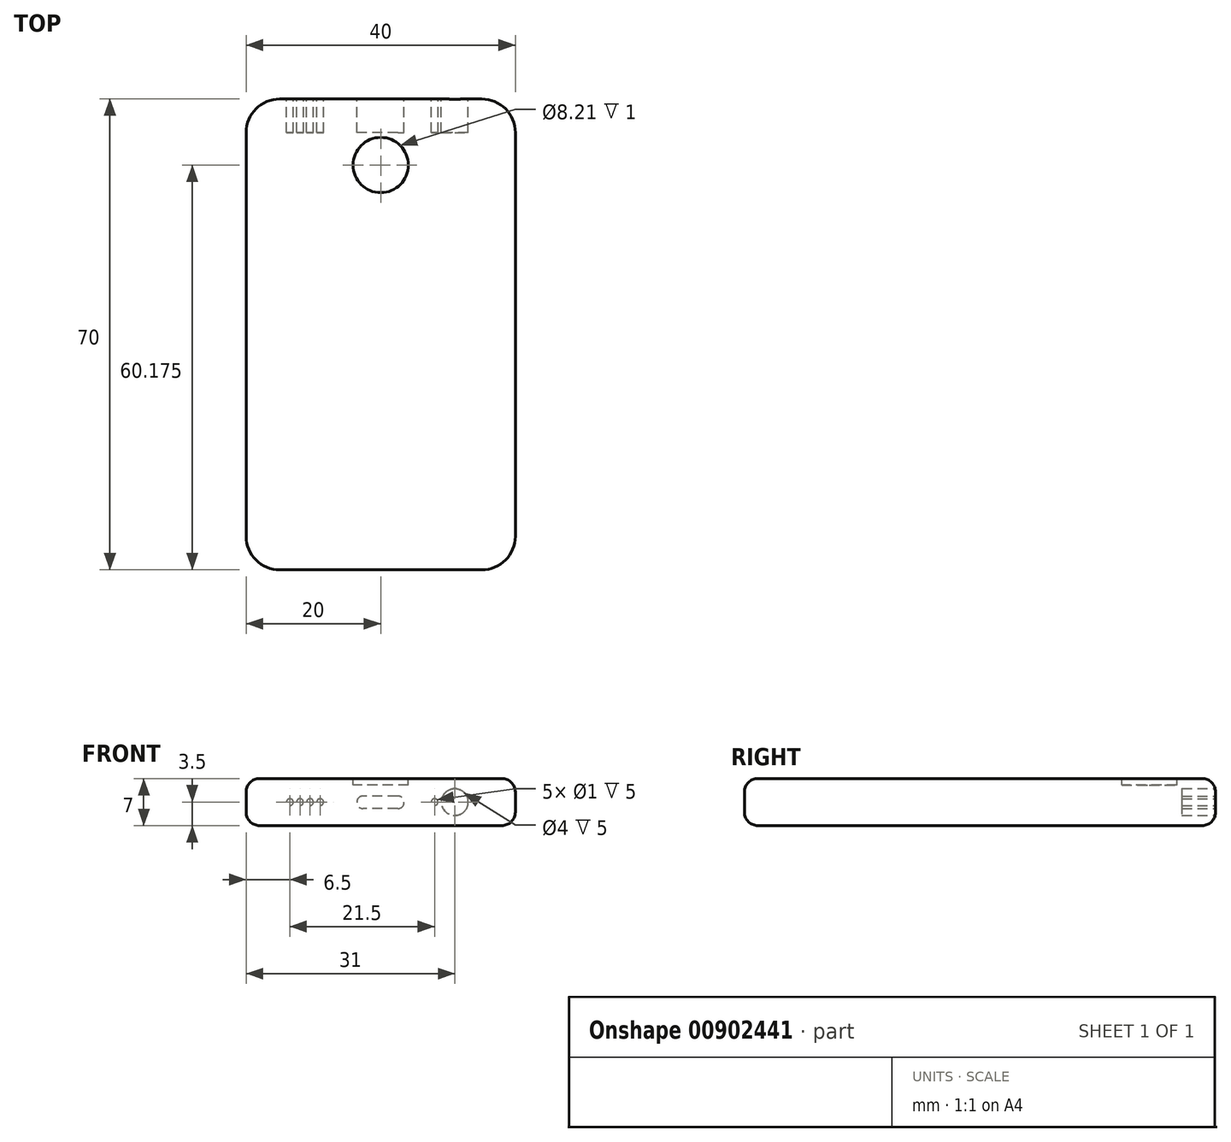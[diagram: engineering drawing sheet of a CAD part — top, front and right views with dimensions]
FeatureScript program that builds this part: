
annotation { "Feature Type Name" : "Feature", "Feature Type Description" : "" }
export const myFeature = defineFeature(function(context is Context, id is Id, definition is map)
    precondition{}
    {
        {
            var Q0;
            Q0=qCreatedBy(makeId("Top.planeOp"),FACE);
            var sketch = newSketch(context, id + "F0", { "sketchPlane" : qUnion([Q0])});
            skLineSegment(sketch, "E0.bottom", {"start": v(0, 0) * mm, "end": v(40, 0) * mm});
            skLineSegment(sketch, "E0.top", {"start": v(0, 70) * mm, "end": v(40, 70) * mm});
            skLineSegment(sketch, "E0.left", {"start": v(0, 0) * mm, "end": v(0, 70) * mm});
            skLineSegment(sketch, "E0.right", {"start": v(40, 0) * mm, "end": v(40, 70) * mm});
            skSolve(sketch);
        }
        {
            var Q0;
            Q0 = qSketchRegion(id + "F0", true);
            extrude(context, id + "F1", {"entities" : qUnion([Q0]), "depth" : 7 * mm, "offsetDistance" : 25 * mm});
        }
        {
            var Q0;
            Q0=makeQuery(id+"F1.opExtrude","SWEPT_EDGE",EDGE,{"disambiguationData":[OSD([sQuery(id+"F0.wireOp",EDGE,"E0.bottom"),sQuery(id+"F0.wireOp",EDGE,"E0.right")])]});
            var Q1;
            Q1=makeQuery(id+"F1.opExtrude","SWEPT_EDGE",EDGE,{"disambiguationData":[OSD([sQuery(id+"F0.wireOp",EDGE,"E0.bottom"),sQuery(id+"F0.wireOp",EDGE,"E0.left")])]});
            var Q2;
            Q2=makeQuery(id+"F1.opExtrude","SWEPT_EDGE",EDGE,{"disambiguationData":[OSD([sQuery(id+"F0.wireOp",EDGE,"E0.top"),sQuery(id+"F0.wireOp",EDGE,"E0.right")])]});
            var Q3;
            Q3=makeQuery(id+"F1.opExtrude","SWEPT_EDGE",EDGE,{"disambiguationData":[OSD([sQuery(id+"F0.wireOp",EDGE,"E0.top"),sQuery(id+"F0.wireOp",EDGE,"E0.left")])]});
            fillet(context, id + "F2", {"entities" : qUnion([Q0, Q1, Q2, Q3]), "radius" : 5 * mm, "tangentPropagation" : true, "allowEdgeOverflow" : false});
        }
        {
            var Q0;
            Q0=makeQuery(id+"F1.opExtrude","SWEPT_FACE",FACE,{"disambiguationData":[OSD([sQuery(id+"F0.wireOp",EDGE,"E0.top")])]});
            var sketch = newSketch(context, id + "F3", { "sketchPlane" : qUnion([Q0])});
            skCircle(sketch, "E1", {"center": v(-31, 3.5) * mm, "radius": 2 * mm});
            skPoint(sketch, "E1.centerSnap0", {"position": v(-35, 3.5) * mm});
            skSolve(sketch);
        }
        {
            var Q0;
            Q0 = qSketchRegion(id + "F3", true);
            extrude(context, id + "F4", {"entities" : qUnion([Q0]), "operationType" : NewBodyOperationType.REMOVE, "oppositeDirection" : true, "depth" : 5 * mm, "offsetDistance" : 25 * mm});
        }
        {
            var Q0;
            Q0=makeQuery(id+"F1.opExtrude","CAP_EDGE",EDGE,{"disambiguationData":[OSD([sQuery(id+"F0.wireOp",EDGE,"E0.top")])],"isStart":false});
            var Q1;
            Q1=makeQuery(id+"F1.opExtrude","CAP_EDGE",EDGE,{"disambiguationData":[OSD([sQuery(id+"F0.wireOp",EDGE,"E0.top")])],"isStart":true});
            fillet(context, id + "F5", {"entities" : qUnion([Q0, Q1]), "radius" : 2 * mm, "tangentPropagation" : true, "allowEdgeOverflow" : false});
        }
        {
            var Q0;
            Q0=makeQuery(id+"F1.opExtrude","CAP_FACE",FACE,{"disambiguationData":[OSD([sQuery(id+"F0.wireOp",EDGE,"E0.bottom"),sQuery(id+"F0.wireOp",EDGE,"E0.top"),sQuery(id+"F0.wireOp",EDGE,"E0.left"),sQuery(id+"F0.wireOp",EDGE,"E0.right")])],"isStart":false});
            var sketch = newSketch(context, id + "F6", { "sketchPlane" : qUnion([Q0])});
            skCircle(sketch, "E2", {"center": v(20, 60.18) * mm, "radius": 4.1 * mm});
            skPoint(sketch, "E2.centerSnap0", {"position": v(20, 68) * mm});
            skSolve(sketch);
        }
        {
            var Q0;
            Q0 = qSketchRegion(id + "F6", true);
            extrude(context, id + "F7", {"entities" : qUnion([Q0]), "operationType" : NewBodyOperationType.REMOVE, "oppositeDirection" : true, "depth" : 1 * mm, "offsetDistance" : 25 * mm});
        }
        {
            var Q0;
            Q0=makeQuery(id+"F5.opFillet","SPLIT",FACE,{"disambiguationData":[OD(0.0)],"derivedFrom":makeQuery(id+"F1.opExtrude","SWEPT_FACE",FACE,{"disambiguationData":[OSD([sQuery(id+"F0.wireOp",EDGE,"E0.top")])]})});
            var sketch = newSketch(context, id + "F8", { "sketchPlane" : qUnion([Q0])});
            skCircle(sketch, "E3", {"center": v(-28, 3.5) * mm, "radius": 0.5 * mm});
            skPoint(sketch, "E3.centerSnap0", {"position": v(-29, 3.5) * mm});
            skSolve(sketch);
        }
        {
            var Q0;
            Q0 = qSketchRegion(id + "F8", true);
            extrude(context, id + "F9", {"entities" : qUnion([Q0]), "operationType" : NewBodyOperationType.REMOVE, "oppositeDirection" : true, "depth" : 5 * mm, "offsetDistance" : 25 * mm});
        }
        {
            var Q0;
            Q0=makeQuery(id+"F5.opFillet","SPLIT",FACE,{"disambiguationData":[OD(0.0)],"derivedFrom":makeQuery(id+"F1.opExtrude","SWEPT_FACE",FACE,{"disambiguationData":[OSD([sQuery(id+"F0.wireOp",EDGE,"E0.top")])]})});
            var sketch = newSketch(context, id + "F10", { "sketchPlane" : qUnion([Q0])});
            skLineSegment(sketch, "E4.bottom", {"start": v(-22.54, 4.4) * mm, "end": v(-17.38, 4.4) * mm});
            skLineSegment(sketch, "E4.top", {"start": v(-22.54, 2.53) * mm, "end": v(-17.38, 2.53) * mm});
            skArc(sketch, "E5", {"start": v(-22.54, 4.4) * mm, "mid": v(-23.48, 3.47) * mm, "end": v(-22.54, 2.53) * mm});
            skArc(sketch, "E6", {"start": v(-17.38, 2.53) * mm, "mid": v(-16.44, 3.47) * mm, "end": v(-17.38, 4.4) * mm});
            skSolve(sketch);
        }
        {
            var Q0;
            Q0 = qSketchRegion(id + "F10", true);
            extrude(context, id + "F11", {"entities" : qUnion([Q0]), "operationType" : NewBodyOperationType.REMOVE, "oppositeDirection" : true, "depth" : 5 * mm, "offsetDistance" : 25 * mm});
        }
        {
            var Q0;
            Q0=makeQuery(id+"F5.opFillet","SPLIT",FACE,{"disambiguationData":[OD(0.0)],"derivedFrom":makeQuery(id+"F1.opExtrude","SWEPT_FACE",FACE,{"disambiguationData":[OSD([sQuery(id+"F0.wireOp",EDGE,"E0.top")])]})});
            var sketch = newSketch(context, id + "F12", { "sketchPlane" : qUnion([Q0])});
            skCircle(sketch, "E7", {"center": v(-6.5, 3.5) * mm, "radius": 0.5 * mm});
            skPoint(sketch, "E7.centerSnap0", {"position": v(-5, 3.5) * mm});
            skCircle(sketch, "E8", {"center": v(-8, 3.5) * mm, "radius": 0.5 * mm});
            skCircle(sketch, "E9", {"center": v(-9.5, 3.5) * mm, "radius": 0.5 * mm});
            skCircle(sketch, "E10", {"center": v(-11, 3.5) * mm, "radius": 0.5 * mm});
            skSolve(sketch);
        }
        {
            var Q0;
            Q0 = qSketchRegion(id + "F12", true);
            extrude(context, id + "F13", {"entities" : qUnion([Q0]), "operationType" : NewBodyOperationType.REMOVE, "oppositeDirection" : true, "depth" : 5 * mm, "offsetDistance" : 25 * mm});
        }
    });
